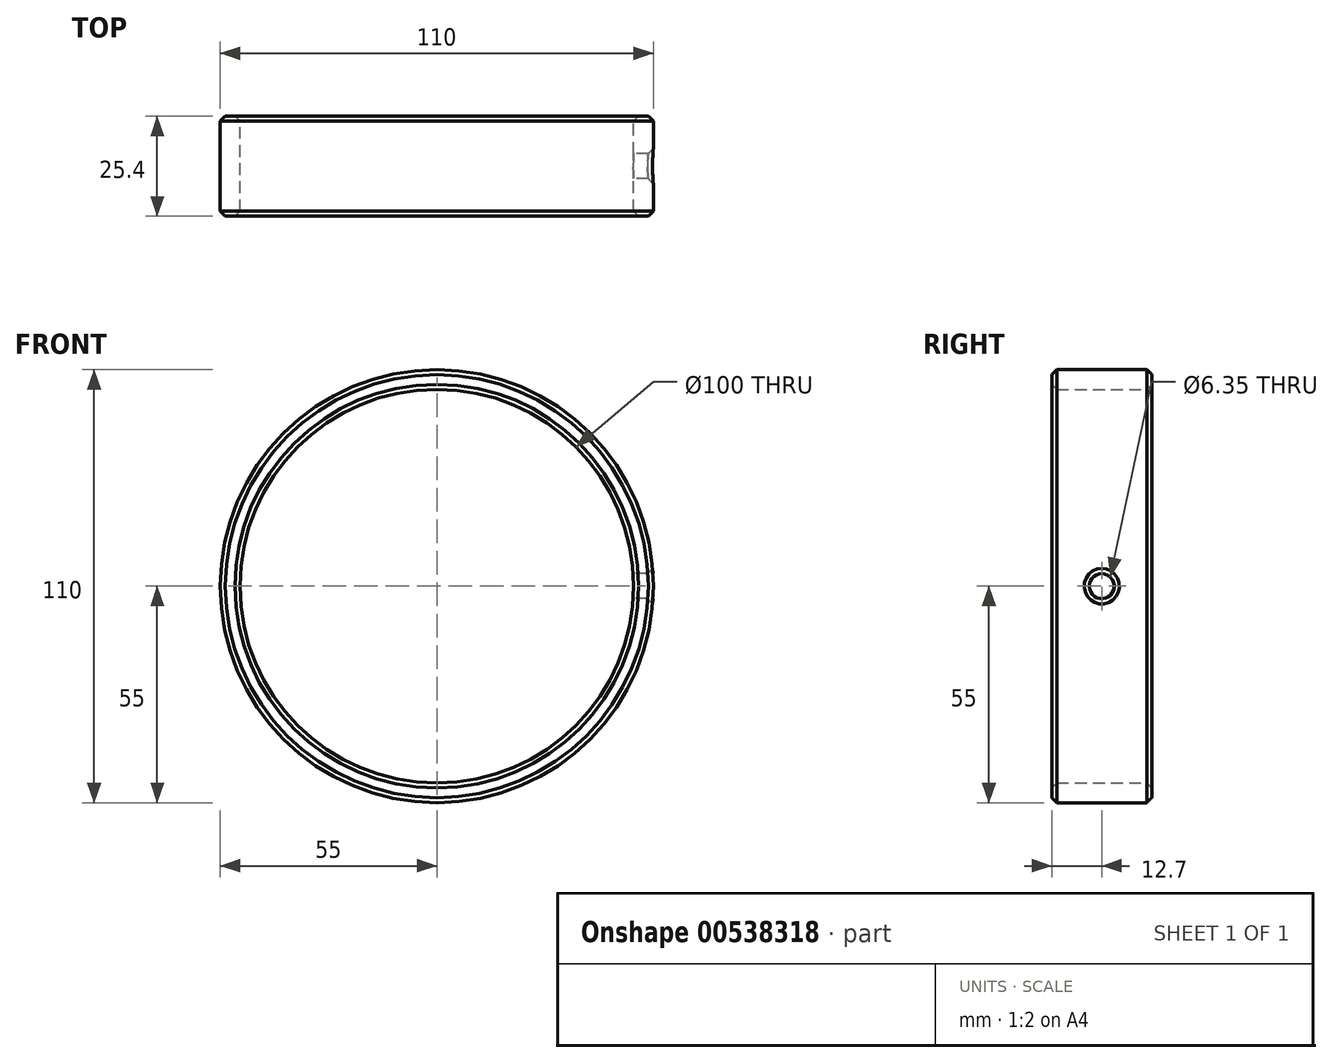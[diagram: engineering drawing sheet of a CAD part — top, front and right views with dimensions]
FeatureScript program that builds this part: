
annotation { "Feature Type Name" : "Feature", "Feature Type Description" : "" }
export const myFeature = defineFeature(function(context is Context, id is Id, definition is map)
    precondition{}
    {
        {
            var Q0;
            Q0=qCreatedBy(makeId("Front.planeOp"),FACE);
            var sketch = newSketch(context, id + "F0", { "sketchPlane" : qUnion([Q0])});
            skCircle(sketch, "E0", {"center": v(0, 0) * mm, "radius": 55 * mm});
            skCircle(sketch, "E1", {"center": v(0, 0) * mm, "radius": 50 * mm});
            skSolve(sketch);
        }
        {
            var Q0;
            Q0=makeQuery(id+"F0.imprint","IMPRINT",FACE,{"disambiguationData":[TD([[makeQuery(id+"F0.imprint","IMPRINT",EDGE,{"derivedFrom":sQuery(id+"F0.wireOp",EDGE,"E0")}),1.0]])]});
            extrude(context, id + "F1", {"entities" : qUnion([Q0]), "depth" : 25.4 * mm, "offsetDistance" : 25.4 * mm});
        }
        {
            var Q0;
            Q0=qCreatedBy(makeId("Right.planeOp"),FACE);
            var sketch = newSketch(context, id + "F2", { "sketchPlane" : qUnion([Q0])});
            skCircle(sketch, "E2", {"center": v(-12.7, 0) * mm, "radius": 3.18 * mm});
            skSolve(sketch);
        }
        {
            var Q0;
            Q0 = qSketchRegion(id + "F2", true);
            extrude(context, id + "F3", {"entities" : qUnion([Q0]), "operationType" : NewBodyOperationType.REMOVE, "endBound" : BoundingType.THROUGH_ALL, "depth" : 25.4 * mm, "offsetDistance" : 25.4 * mm});
        }
        {
            var Q0;
            Q0=makeQuery(id+"F3.boolean.opBoolean","INTERSECT",EDGE,{"derivedFrom":[makeQuery(id+"F1.opExtrude","SWEPT_FACE",FACE,{"disambiguationData":[OSD([sQuery(id+"F0.wireOp",EDGE,"E0")])]}),makeQuery(id+"F3.opExtrude","SWEPT_FACE",FACE,{"disambiguationData":[OSD([sQuery(id+"F2.wireOp",EDGE,"E2")])]})]});
            chamfer(context, id + "F4", {"entities" : qUnion([Q0]), "width" : 1.27 * mm, "tangentPropagation" : true});
        }
        {
            var Q0;
            Q0=makeQuery(id+"F1.opExtrude","CAP_EDGE",EDGE,{"disambiguationData":[OSD([sQuery(id+"F0.wireOp",EDGE,"E1")])],"isStart":true});
            var Q1;
            Q1=makeQuery(id+"F1.opExtrude","CAP_EDGE",EDGE,{"disambiguationData":[OSD([sQuery(id+"F0.wireOp",EDGE,"E0")])],"isStart":false});
            var Q2;
            Q2=makeQuery(id+"F1.opExtrude","CAP_EDGE",EDGE,{"disambiguationData":[OSD([sQuery(id+"F0.wireOp",EDGE,"E0")])],"isStart":true});
            var Q3;
            Q3=makeQuery(id+"F1.opExtrude","CAP_EDGE",EDGE,{"disambiguationData":[OSD([sQuery(id+"F0.wireOp",EDGE,"E1")])],"isStart":false});
            chamfer(context, id + "F5", {"entities" : qUnion([Q0, Q1, Q2, Q3]), "width" : 1.27 * mm, "tangentPropagation" : true});
        }
    });
